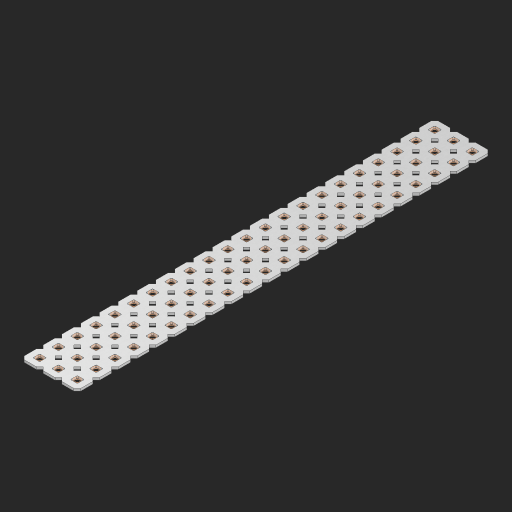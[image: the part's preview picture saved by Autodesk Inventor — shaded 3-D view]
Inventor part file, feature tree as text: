
AUTODESK INVENTOR PART (.ipt)
format: ipt  version: 2023 (Build 270158000, 158)  size: 1,041,920 bytes
history: native  units: in
note: dims shown in document units (in); Inventor stores cm internally (conversion verified against a paired STEP export)
features: other x67, extrude x65, sketch x2, pattern_linear x1
ambient origin geometry x8: Origin, YZ Plane, XZ Plane, XY Plane, X Axis, Y Axis, Z Axis, Center Point
bodies: Solid1 (feature_tree), Body (feature_tree)
feature tree (135):
  pattern_linear  "Rectangular Pattern1"  Spacing1=0.09in  [1 undecoded]
  sketch  "Sketch1"  dims[d1=0.5in]
  sketch  "Sketch2"  dims[d2=0.182in d3=0.09in d4=0.09in d5=0.09in d6=0.09in d7=0.09in d8=0.09in d9=0.09in d10=0.09in d11=0.02in d13=0.0in d14=0.172in d15=0.0625in d16=0.0in d19=0.5in d22=0.5in]
  other  "Srf1"
  other  "Srf126"
  other  "Srf127"
  other  "Srf128"
  other  "Srf129"
  other  "Srf130"
  other  "Srf131"
  other  "Srf250"
  other  "Srf251"
  other  "Srf252"
  other  "Srf253"
  other  "Srf254"
  other  "Srf255"
  other  "Srf256"
  other  "Srf257"
  other  "Srf258"
  other  "Srf259"
  other  "Srf260"
  other  "Srf261"
  other  "Srf262"
  other  "Srf263"
  other  "Srf264"
  other  "Srf268"
  other  "Srf269"
  other  "Srf270"
  other  "Srf271"
  other  "Srf272"
  other  "Srf273"
  other  "Srf274"
  other  "Srf275"
  other  "Srf276"
  other  "Srf277"
  other  "Srf278"
  other  "Srf279"
  other  "Srf280"
  other  "Srf281"
  other  "Srf282"
  other  "Srf283"
  other  "Srf284"
  other  "Srf285"
  other  "Srf286"
  other  "Srf287"
  other  "Srf288"
  other  "Srf289"
  other  "Srf293"
  other  "Srf294"
  other  "Srf295"
  other  "Srf296"
  other  "Srf297"
  other  "Srf298"
  other  "Srf299"
  other  "Srf300"
  other  "Srf301"
  other  "Srf302"
  other  "Srf303"
  other  "Srf304"
  other  "Srf305"
  other  "Srf306"
  other  "Srf307"
  other  "Srf308"
  other  "Srf309"
  other  "Srf310"
  other  "Srf311"
  other  "Srf312"
  other  "Srf313"
  other  "Srf314"
  other  "Circle"
  extrude  "ExtrusionSrf126"  Depth=0.09in
  extrude  "ExtrusionSrf127"  Depth=0.09in
  extrude  "ExtrusionSrf128"  Depth=0.09in
  extrude  "ExtrusionSrf129"  Depth=0.09in
  extrude  "ExtrusionSrf130"  Depth=0.09in
  extrude  "ExtrusionSrf131"  Depth=0.09in
  extrude  "ExtrusionSrf250"  Depth=0.09in
  extrude  "ExtrusionSrf251"  Depth=0.02in
  extrude  "ExtrusionSrf252"  TaperAngle=0.0deg  [1 undecoded]
  extrude  "ExtrusionSrf253"  Depth=0.5in
  extrude  "ExtrusionSrf254"  Depth=0.0625in TaperAngle=0.0deg
  extrude  "ExtrusionSrf255"  Depth=0.5in
  extrude  "ExtrusionSrf256"  Depth=0.5in
  extrude  "ExtrusionSrf257"  [1 undecoded]
  extrude  "ExtrusionSrf258"  [1 undecoded]
  extrude  "ExtrusionSrf259"  [1 undecoded]
  extrude  "ExtrusionSrf260"  [1 undecoded]
  extrude  "ExtrusionSrf261"  [1 undecoded]
  extrude  "ExtrusionSrf262"  [1 undecoded]
  extrude  "ExtrusionSrf263"  [1 undecoded]
  extrude  "ExtrusionSrf264"  [1 undecoded]
  extrude  "ExtrusionSrf268"  [1 undecoded]
  extrude  "ExtrusionSrf269"  [1 undecoded]
  extrude  "ExtrusionSrf270"  [1 undecoded]
  extrude  "ExtrusionSrf271"  [1 undecoded]
  extrude  "ExtrusionSrf272"  [1 undecoded]
  extrude  "ExtrusionSrf273"  [1 undecoded]
  extrude  "ExtrusionSrf274"  [1 undecoded]
  extrude  "ExtrusionSrf275"  [1 undecoded]
  extrude  "ExtrusionSrf276"  [1 undecoded]
  extrude  "ExtrusionSrf277"  [1 undecoded]
  extrude  "ExtrusionSrf278"  [1 undecoded]
  extrude  "ExtrusionSrf279"  [1 undecoded]
  extrude  "ExtrusionSrf280"  [1 undecoded]
  extrude  "ExtrusionSrf281"  [1 undecoded]
  extrude  "ExtrusionSrf282"  [1 undecoded]
  extrude  "ExtrusionSrf283"  [1 undecoded]
  extrude  "ExtrusionSrf284"  [1 undecoded]
  extrude  "ExtrusionSrf285"  [1 undecoded]
  extrude  "ExtrusionSrf286"  [1 undecoded]
  extrude  "ExtrusionSrf287"  [1 undecoded]
  extrude  "ExtrusionSrf288"  [1 undecoded]
  extrude  "ExtrusionSrf289"  [1 undecoded]
  extrude  "ExtrusionSrf293"  [1 undecoded]
  extrude  "ExtrusionSrf294"  [1 undecoded]
  extrude  "ExtrusionSrf295"  [1 undecoded]
  extrude  "ExtrusionSrf296"  [1 undecoded]
  extrude  "ExtrusionSrf297"  [1 undecoded]
  extrude  "ExtrusionSrf298"  [1 undecoded]
  extrude  "ExtrusionSrf299"  [1 undecoded]
  extrude  "ExtrusionSrf300"  [1 undecoded]
  extrude  "ExtrusionSrf301"  [1 undecoded]
  extrude  "ExtrusionSrf302"  [1 undecoded]
  extrude  "ExtrusionSrf303"  [1 undecoded]
  extrude  "ExtrusionSrf304"  [1 undecoded]
  extrude  "ExtrusionSrf305"  [1 undecoded]
  extrude  "ExtrusionSrf306"  [1 undecoded]
  extrude  "ExtrusionSrf307"  [1 undecoded]
  extrude  "ExtrusionSrf308"  [1 undecoded]
  extrude  "ExtrusionSrf309"  [1 undecoded]
  extrude  "ExtrusionSrf310"  [1 undecoded]
  extrude  "ExtrusionSrf311"  [1 undecoded]
  extrude  "ExtrusionSrf312"  [1 undecoded]
  extrude  "ExtrusionSrf313"  [1 undecoded]
  extrude  "ExtrusionSrf314"  [1 undecoded]
note: 54 required parameter values undecoded (feature->parameter linkage not recoverable at this tier; creation-order binding heuristic only, values carry confidence <= 0.55)
